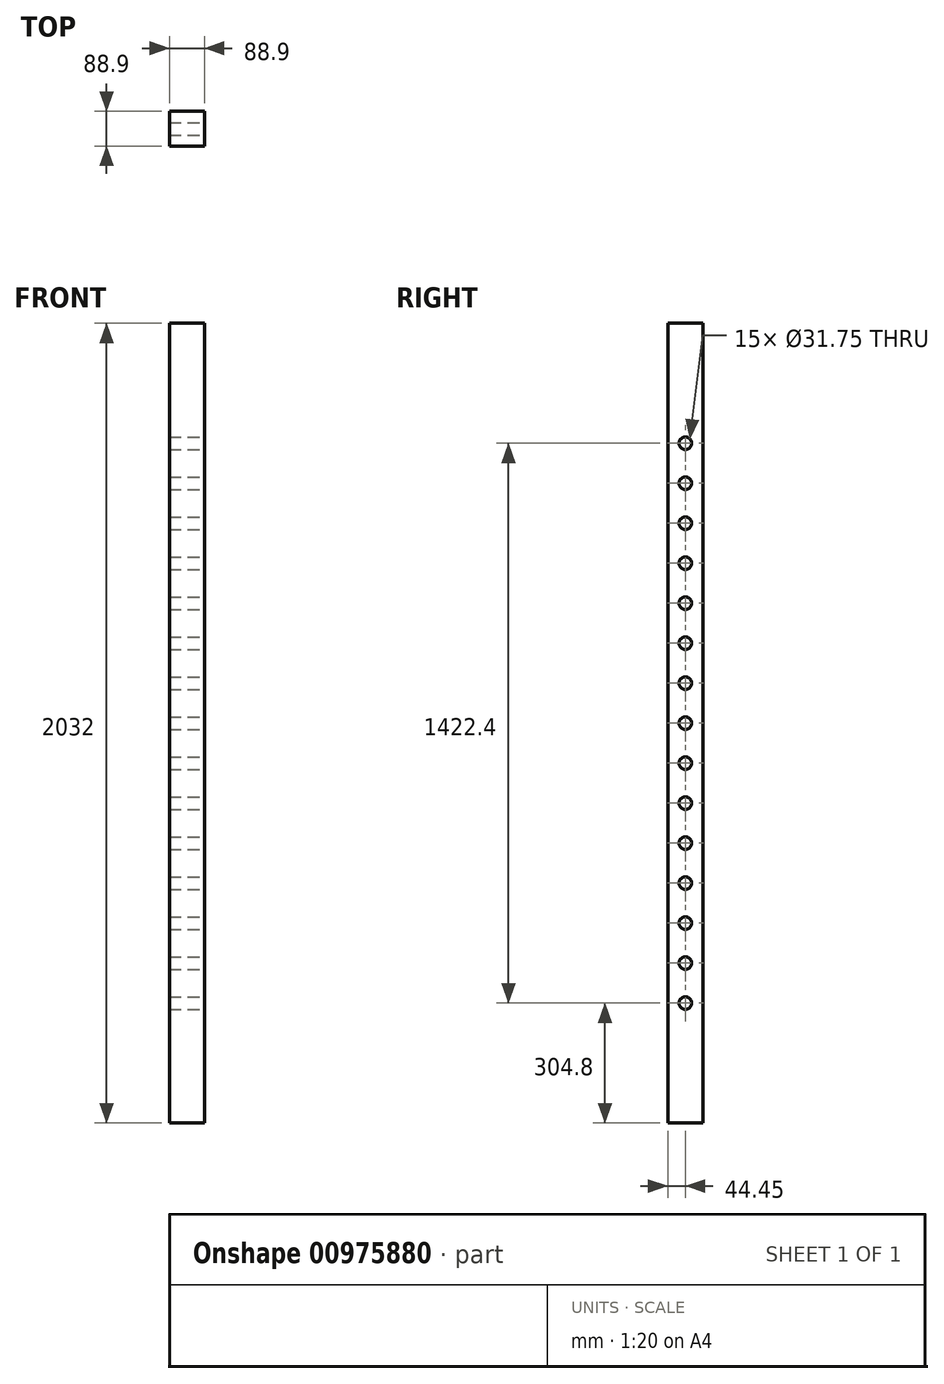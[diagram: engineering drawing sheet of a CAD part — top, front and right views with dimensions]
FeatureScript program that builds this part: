
annotation { "Feature Type Name" : "Feature", "Feature Type Description" : "" }
export const myFeature = defineFeature(function(context is Context, id is Id, definition is map)
    precondition{}
    {
        {
            var Q0;
            Q0=qCreatedBy(makeId("Right.planeOp"),FACE);
            var sketch = newSketch(context, id + "F0", { "sketchPlane" : qUnion([Q0])});
            skLineSegment(sketch, "E0.bottom", {"start": v(44.45, 1016) * mm, "end": v(-44.45, 1016) * mm});
            skLineSegment(sketch, "E0.top", {"start": v(44.45, -1016) * mm, "end": v(-44.45, -1016) * mm});
            skLineSegment(sketch, "E0.left", {"start": v(44.45, 1016) * mm, "end": v(44.45, -1016) * mm});
            skLineSegment(sketch, "E0.right", {"start": v(-44.45, 1016) * mm, "end": v(-44.45, -1016) * mm});
            skPoint(sketch, "E0.middle", {"position": v(0, 0) * mm});
            skCircle(sketch, "E1", {"center": v(0, -711.2) * mm, "radius": 15.88 * mm});
            skCircle(sketch, "E2.0.1.0", {"center": v(0, -609.6) * mm, "radius": 15.88 * mm});
            skCircle(sketch, "E2.0.2.0", {"center": v(0, -508) * mm, "radius": 15.88 * mm});
            skCircle(sketch, "E2.0.3.0", {"center": v(0, -406.4) * mm, "radius": 15.88 * mm});
            skCircle(sketch, "E2.0.4.0", {"center": v(0, -304.8) * mm, "radius": 15.88 * mm});
            skCircle(sketch, "E2.0.5.0", {"center": v(0, -203.2) * mm, "radius": 15.88 * mm});
            skCircle(sketch, "E2.0.6.0", {"center": v(0, -101.6) * mm, "radius": 15.88 * mm});
            skCircle(sketch, "E2.0.7.0", {"center": v(0, 0) * mm, "radius": 15.88 * mm});
            skCircle(sketch, "E2.0.8.0", {"center": v(0, 101.6) * mm, "radius": 15.88 * mm});
            skCircle(sketch, "E2.0.9.0", {"center": v(0, 203.2) * mm, "radius": 15.88 * mm});
            skCircle(sketch, "E2.0.10.0", {"center": v(0, 304.8) * mm, "radius": 15.88 * mm});
            skCircle(sketch, "E2.0.11.0", {"center": v(0, 406.4) * mm, "radius": 15.88 * mm});
            skCircle(sketch, "E2.0.12.0", {"center": v(0, 508) * mm, "radius": 15.88 * mm});
            skCircle(sketch, "E2.0.13.0", {"center": v(0, 609.6) * mm, "radius": 15.88 * mm});
            skLineSegment(sketch, "E2.direction1", {"start": v(0, -711.2) * mm, "end": v(25.4, -711.2) * mm, "construction": true});
            skLineSegment(sketch, "E2.direction2", {"start": v(0, -711.2) * mm, "end": v(0, -609.6) * mm, "construction": true});
            skCircle(sketch, "E3.0.0.14", {"center": v(0, 711.2) * mm, "radius": 15.88 * mm});
            skSolve(sketch);
        }
        {
            var Q0;
            Q0=makeQuery(id+"F0.imprint","IMPRINT",FACE,{"disambiguationData":[TD([[makeQuery(id+"F0.imprint","IMPRINT",EDGE,{"derivedFrom":sQuery(id+"F0.wireOp",EDGE,"E0.bottom")}),1.0]])]});
            extrude(context, id + "F1", {"entities" : qUnion([Q0]), "oppositeDirection" : true, "depth" : 88.9 * mm, "offsetDistance" : 25.4 * mm});
        }
    });
